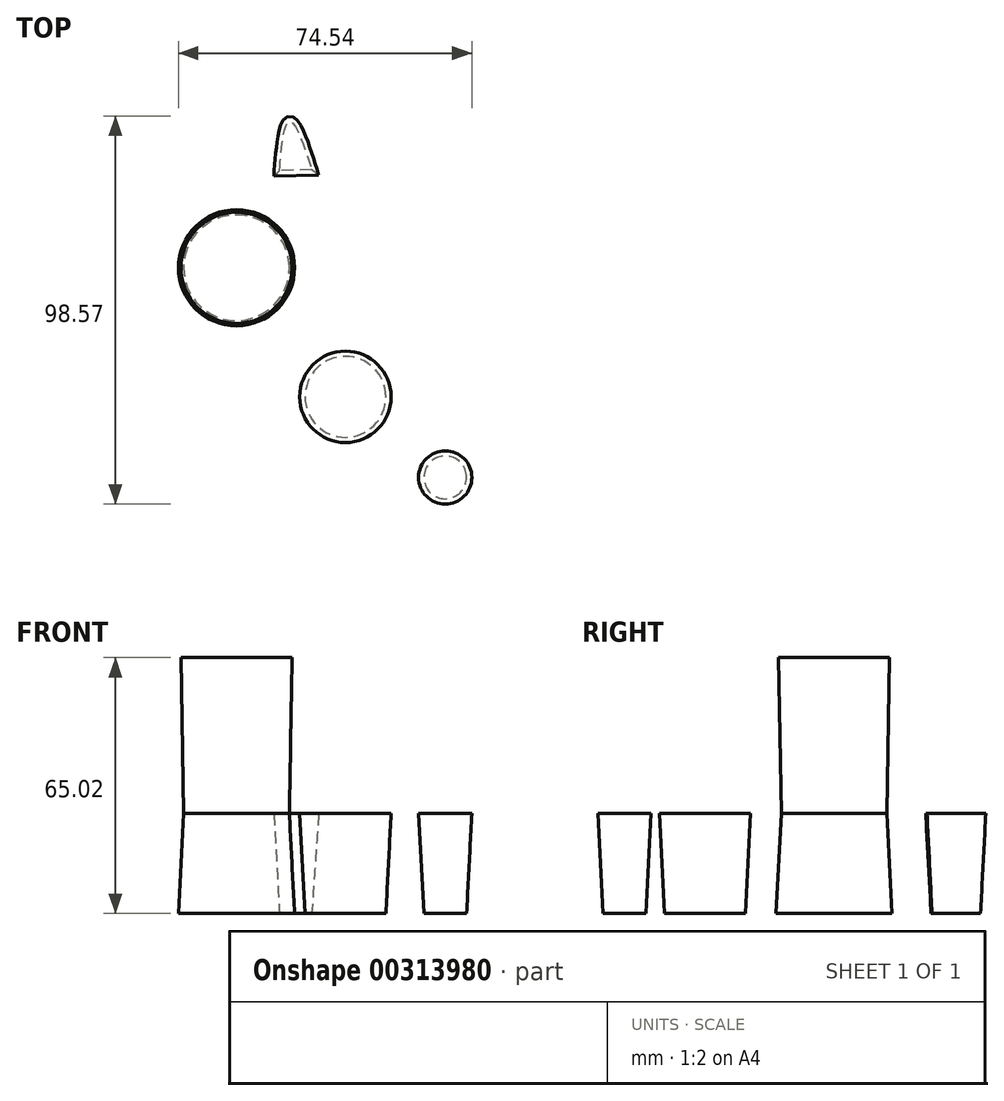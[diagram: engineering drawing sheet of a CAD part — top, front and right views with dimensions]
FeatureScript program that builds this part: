
annotation { "Feature Type Name" : "Feature", "Feature Type Description" : "" }
export const myFeature = defineFeature(function(context is Context, id is Id, definition is map)
    precondition{}
    {
        {
            var Q0;
            Q0=qCreatedBy(makeId("Top.planeOp"),FACE);
            var sketch = newSketch(context, id + "F0", { "sketchPlane" : qUnion([Q0])});
            skFitSpline(sketch, "E0", {"points": [v(-53.73, 62.33) * mm, v(-71.64, 63.03) * mm, v(-70.7, 46.28) * mm, v(-55.36, 42.56) * mm, v(-46.75, 27.68) * mm, v(-62.1, 16.51) * mm, v(-69.78, 18.84) * mm], "startDerivative": vector(-122.23, 38) * mm, "endDerivative": vector(-53.07, 33.74) * mm});
            skFitSpline(sketch, "E1", {"points": [v(-41.4, 42.1) * mm, v(-41.63, 17.21) * mm], "startDerivative": vector(-0.23, -24.89) * mm, "endDerivative": vector(-0.23, -24.89) * mm});
            skFitSpline(sketch, "E2", {"points": [v(-35.12, 41.4) * mm, v(-34.89, 16.75) * mm, v(-23.72, 16.28) * mm], "startDerivative": vector(-7.79, -53.23) * mm, "endDerivative": vector(33.25, 6.9) * mm});
            skFitSpline(sketch, "E3", {"points": [v(-21.86, 40.7) * mm, v(-12.8, 16.28) * mm, v(-6.28, 40.7) * mm], "startDerivative": vector(19.24, -73.08) * mm, "endDerivative": vector(11.91, 73.45) * mm});
            skFitSpline(sketch, "E4", {"points": [v(0, 40.7) * mm, v(0, 16.28) * mm], "startDerivative": vector(0, -24.42) * mm, "endDerivative": vector(0, -24.42) * mm});
            skFitSpline(sketch, "E5", {"points": [v(6.05, 16.28) * mm, v(9.3, 41.17) * mm, v(18.6, 16.28) * mm], "startDerivative": vector(3.71, 75.03) * mm, "endDerivative": vector(21.32, -74.32) * mm});
            skFitSpline(sketch, "E6", {"points": [v(6.66, 28.6) * mm, v(15, 28.84) * mm], "startDerivative": vector(8.35, 0.24) * mm, "endDerivative": vector(8.35, 0.24) * mm});
            skCircle(sketch, "E7", {"center": v(48.84, -49.3) * mm, "radius": 5.43 * mm});
            skCircle(sketch, "E8", {"center": v(23.5, -28.84) * mm, "radius": 10.28 * mm});
            skCircle(sketch, "E9", {"center": v(-4.19, 3.95) * mm, "radius": 12.1 * mm});
            skSolve(sketch);
        }
        {
            var Q0;
            Q0 = qSketchRegion(id + "F0", true);
            extrude(context, id + "F1", {"entities" : qUnion([Q0]), "depth" : 25.4 * mm, "hasDraft" : true, "draftAngle" : 3 * degree});
        }
        {
            var Q0;
            Q0=makeQuery(id+"F1.opExtrude","CAP_FACE",FACE,{"disambiguationData":[OSD([sQuery(id+"F0.wireOp",EDGE,"E9")])],"isStart":false});
            extrude(context, id + "F2", {"entities" : qUnion([Q0]), "operationType" : NewBodyOperationType.ADD, "depth" : 39.62 * mm, "hasDraft" : true, "draftAngle" : 1 * degree, "hasSecondDirection" : true, "secondDirectionOppositeDirection" : true, "secondDirectionDepth" : 25.4 * mm, "hasSecondDirectionDraft" : true, "secondDirectionDraftAngle" : 3 * degree});
        }
    });
